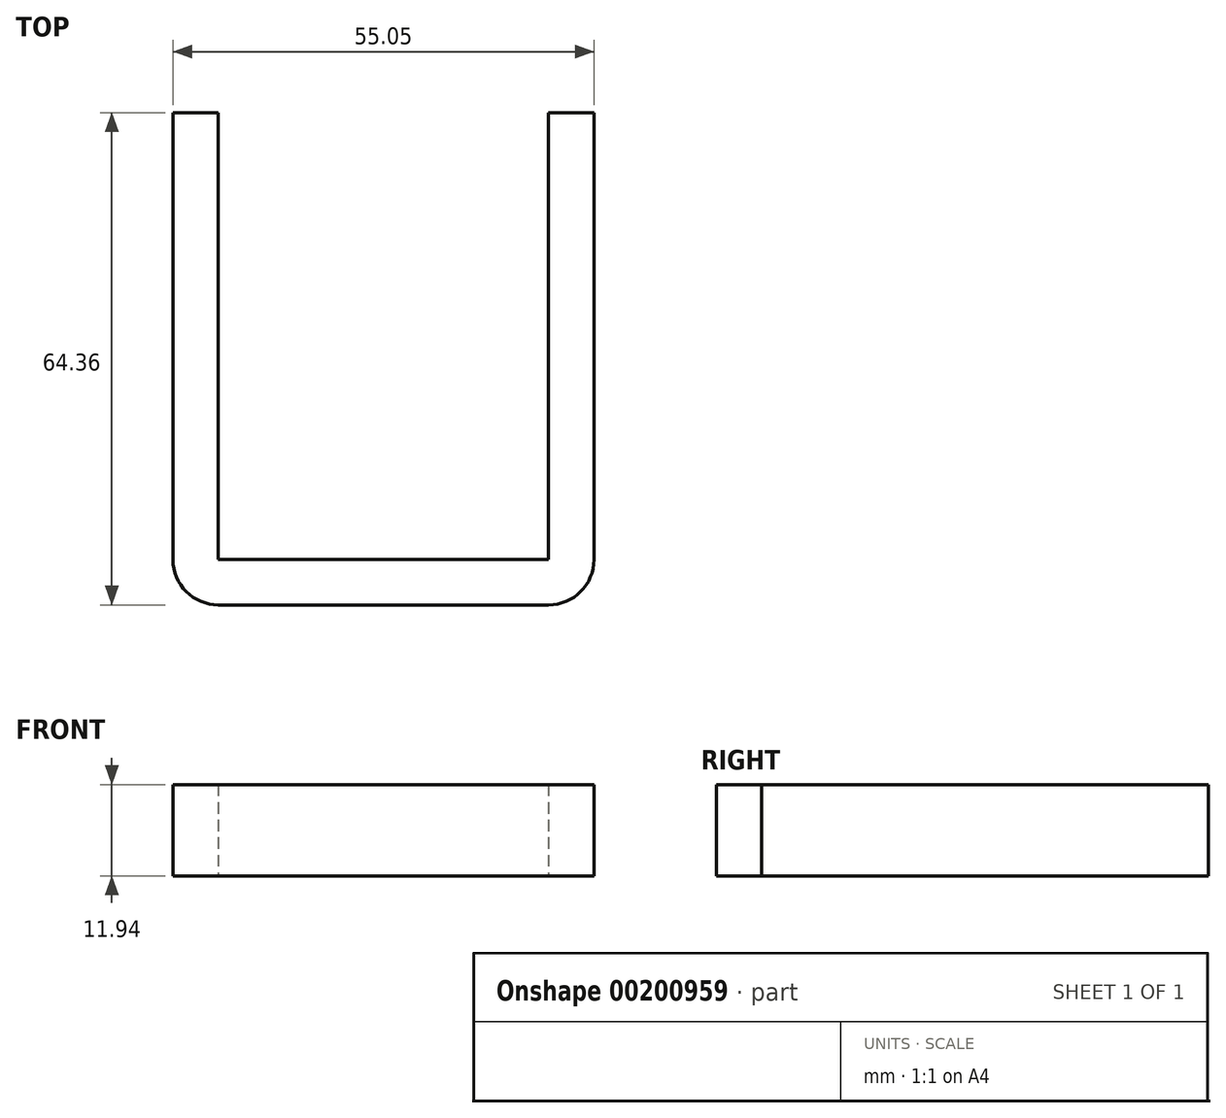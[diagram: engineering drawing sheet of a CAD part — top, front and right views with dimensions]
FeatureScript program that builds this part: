
annotation { "Feature Type Name" : "Feature", "Feature Type Description" : "" }
export const myFeature = defineFeature(function(context is Context, id is Id, definition is map)
    precondition{}
    {
        {
            var Q0;
            Q0=qCreatedBy(makeId("Top.planeOp"),FACE);
            var sketch = newSketch(context, id + "F0", { "sketchPlane" : qUnion([Q0])});
            skLineSegment(sketch, "E0.bottom", {"start": v(-27.97, 9.06) * mm, "end": v(15.2, 9.06) * mm});
            skLineSegment(sketch, "E0.top", {"start": v(-27.97, 3.12) * mm, "end": v(15.2, 3.12) * mm});
            skLineSegment(sketch, "E0.left", {"start": v(-27.97, 9.06) * mm, "end": v(-27.97, 3.12) * mm});
            skLineSegment(sketch, "E0.right", {"start": v(15.2, 9.06) * mm, "end": v(15.2, 3.12) * mm});
            skArc(sketch, "E1", {"start": v(15.2, 3.12) * mm, "mid": v(19.4, 4.86) * mm, "end": v(21.14, 9.06) * mm});
            skArc(sketch, "E2", {"start": v(-27.97, 3.12) * mm, "mid": v(-32.17, 4.86) * mm, "end": v(-33.9, 9.06) * mm});
            skLineSegment(sketch, "E3.bottom", {"start": v(-27.97, 9.06) * mm, "end": v(-33.9, 9.06) * mm});
            skLineSegment(sketch, "E3.top", {"start": v(-27.97, 67.48) * mm, "end": v(-33.9, 67.48) * mm});
            skLineSegment(sketch, "E3.left", {"start": v(-27.97, 9.06) * mm, "end": v(-27.97, 67.48) * mm});
            skLineSegment(sketch, "E3.right", {"start": v(-33.9, 9.06) * mm, "end": v(-33.9, 67.48) * mm});
            skPoint(sketch, "E4.oppositeSnap0", {"position": v(-30.94, 67.48) * mm});
            skLineSegment(sketch, "E4.bottom", {"start": v(15.2, 9.06) * mm, "end": v(21.15, 9.06) * mm});
            skLineSegment(sketch, "E4.top", {"start": v(15.2, 67.48) * mm, "end": v(21.15, 67.48) * mm});
            skLineSegment(sketch, "E4.left", {"start": v(15.2, 9.06) * mm, "end": v(15.2, 67.48) * mm});
            skLineSegment(sketch, "E4.right", {"start": v(21.15, 9.06) * mm, "end": v(21.15, 67.48) * mm});
            skSolve(sketch);
        }
        {
            var Q0;
            Q0 = qSketchRegion(id + "F0", true);
            extrude(context, id + "F1", {"entities" : qUnion([Q0]), "depth" : 11.94 * mm});
        }
    });
